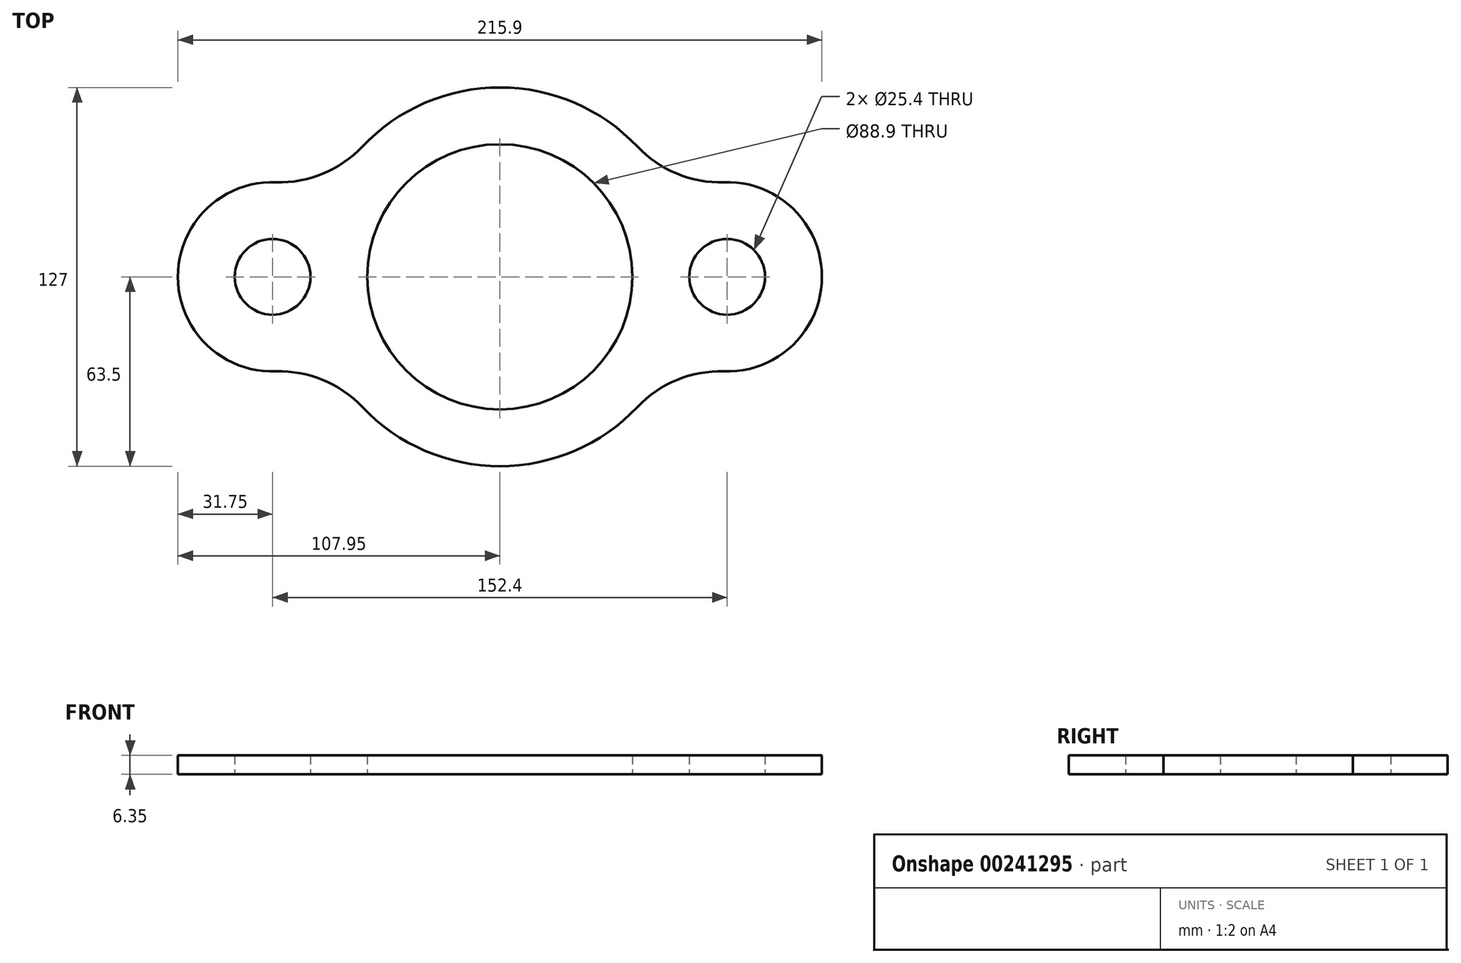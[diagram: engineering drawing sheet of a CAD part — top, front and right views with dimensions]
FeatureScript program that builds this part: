
annotation { "Feature Type Name" : "Feature", "Feature Type Description" : "" }
export const myFeature = defineFeature(function(context is Context, id is Id, definition is map)
    precondition{}
    {
        {
            var Q0;
            Q0=qCreatedBy(makeId("Top.planeOp"),FACE);
            var sketch = newSketch(context, id + "F0", { "sketchPlane" : qUnion([Q0])});
            skCircle(sketch, "E0", {"center": v(0, 0) * mm, "radius": 44.45 * mm});
            skPoint(sketch, "E1", {"position": v(76.2, 0) * mm});
            skCircle(sketch, "E2", {"center": v(76.2, 0) * mm, "radius": 12.7 * mm});
            skCircle(sketch, "E3", {"center": v(-76.2, 0) * mm, "radius": 12.7 * mm});
            skArc(sketch, "E4", {"start": v(-46.14, -43.63) * mm, "mid": v(0, -63.5) * mm, "end": v(46.14, -43.63) * mm});
            skArc(sketch, "E5", {"start": v(-75.12, 31.73) * mm, "mid": v(-107.95, 0) * mm, "end": v(-75.12, -31.73) * mm});
            skArc(sketch, "E6", {"start": v(75.12, -31.73) * mm, "mid": v(107.95, 0) * mm, "end": v(75.12, 31.73) * mm});
            skArc(sketch, "E7.trimOffspring", {"start": v(46.14, 43.63) * mm, "mid": v(0, 63.5) * mm, "end": v(-46.14, 43.63) * mm});
            skArc(sketch, "E8.filletArc", {"start": v(-75.12, 31.73) * mm, "mid": v(-59.35, 34.56) * mm, "end": v(-46.14, 43.63) * mm});
            skArc(sketch, "E9.filletArc", {"start": v(46.14, 43.63) * mm, "mid": v(59.35, 34.56) * mm, "end": v(75.12, 31.73) * mm});
            skArc(sketch, "E10.filletArc", {"start": v(75.12, -31.73) * mm, "mid": v(59.35, -34.56) * mm, "end": v(46.14, -43.63) * mm});
            skArc(sketch, "E11.filletArc", {"start": v(-46.14, -43.63) * mm, "mid": v(-59.35, -34.56) * mm, "end": v(-75.12, -31.73) * mm});
            skSolve(sketch);
        }
        {
            var Q0;
            Q0=makeQuery(id+"F0.imprint","IMPRINT",FACE,{"disambiguationData":[TD([[makeQuery(id+"F0.imprint","IMPRINT",EDGE,{"derivedFrom":sQuery(id+"F0.wireOp",EDGE,"E0")}),-1.0]])]});
            extrude(context, id + "F1", {"entities" : qUnion([Q0]), "depth" : 6.35 * mm});
        }
    });
